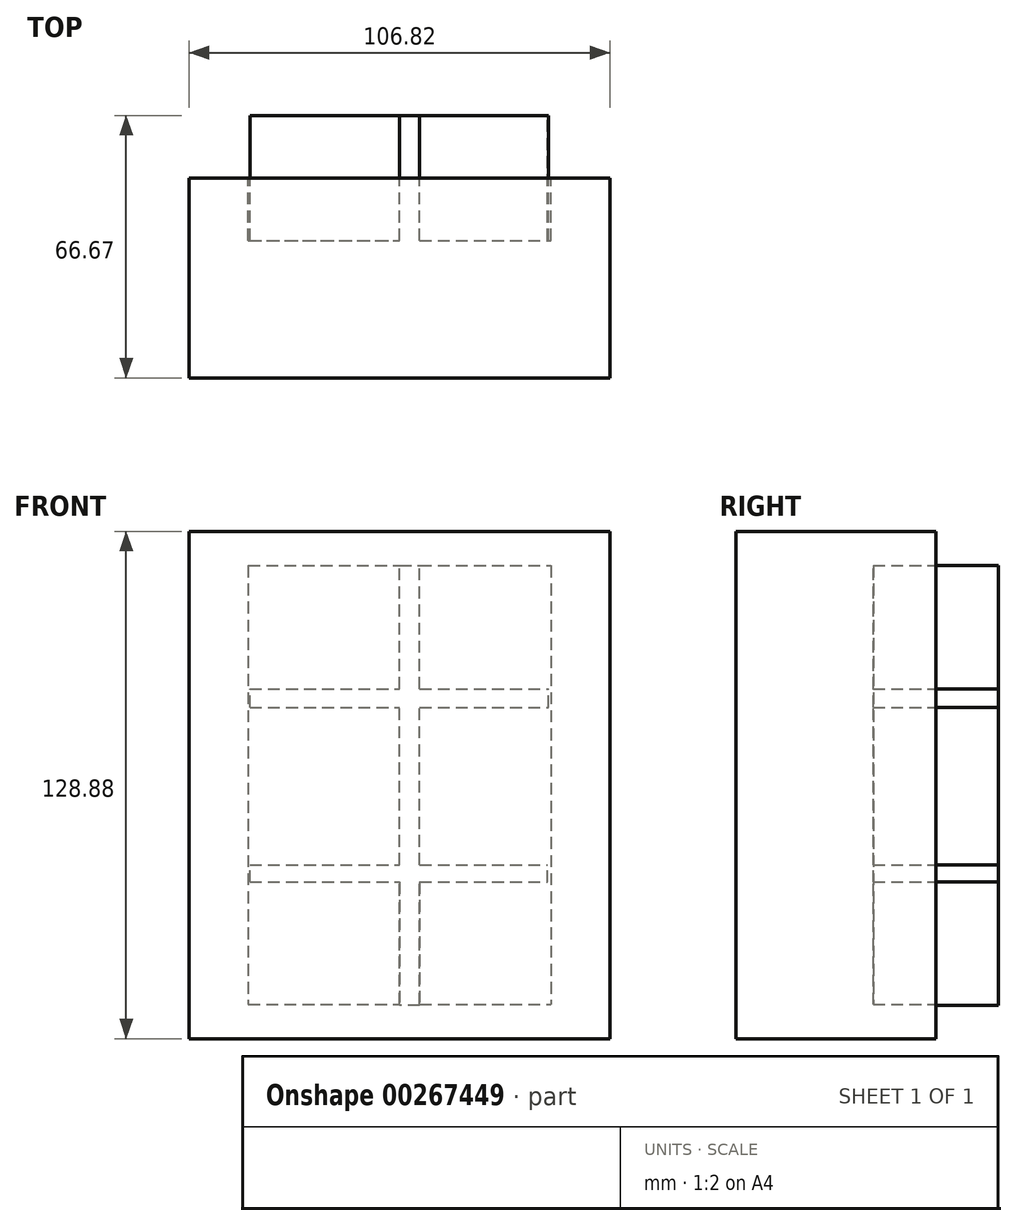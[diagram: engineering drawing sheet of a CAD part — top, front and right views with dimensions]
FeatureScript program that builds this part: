
annotation { "Feature Type Name" : "Feature", "Feature Type Description" : "" }
export const myFeature = defineFeature(function(context is Context, id is Id, definition is map)
    precondition{}
    {
        {
            var Q0;
            Q0=qCreatedBy(makeId("Front.planeOp"),FACE);
            var sketch = newSketch(context, id + "F0", { "sketchPlane" : qUnion([Q0])});
            skLineSegment(sketch, "E0.bottom", {"start": v(-38.43, 55.77) * mm, "end": v(38.43, 55.77) * mm});
            skLineSegment(sketch, "E0.top", {"start": v(-38.43, -55.77) * mm, "end": v(38.43, -55.77) * mm});
            skLineSegment(sketch, "E0.left", {"start": v(-38.43, 55.77) * mm, "end": v(-38.43, -55.77) * mm});
            skLineSegment(sketch, "E0.right", {"start": v(38.43, 55.77) * mm, "end": v(38.43, -55.77) * mm});
            skPoint(sketch, "E0.middle", {"position": v(0, 0) * mm});
            skSolve(sketch);
        }
        {
            var Q0;
            Q0 = qSketchRegion(id + "F0", true);
            extrude(context, id + "F1", {"entities" : qUnion([Q0]), "depth" : 25.4 * mm});
        }
        {
            var Q0;
            Q0=makeQuery(id+"F1.opExtrude","CAP_FACE",FACE,{"disambiguationData":[OSD([sQuery(id+"F0.wireOp",EDGE,"E0.bottom"),sQuery(id+"F0.wireOp",EDGE,"E0.top"),sQuery(id+"F0.wireOp",EDGE,"E0.left"),sQuery(id+"F0.wireOp",EDGE,"E0.right")])],"isStart":false});
            var sketch = newSketch(context, id + "F2", { "sketchPlane" : qUnion([Q0])});
            skLineSegment(sketch, "E1", {"start": v(-38.43, 23.85) * mm, "end": v(38.43, 23.85) * mm});
            skLineSegment(sketch, "E2", {"start": v(-38.43, -19.12) * mm, "end": v(38.43, -19.12) * mm});
            skLineSegment(sketch, "E3", {"start": v(0, 55.77) * mm, "end": v(0, -55.77) * mm});
            skSolve(sketch);
        }
        {
            var Q0;
            Q0 = qSketchRegion(id + "F2", true);
            var Q1;
            {var subQ0=sQuery(id+"F2.wireOp",EDGE,"E1");var subQ1=makeQuery(id+"F1.opExtrude","CAP_EDGE",EDGE,{"disambiguationData":[OSD([sQuery(id+"F0.wireOp",EDGE,"E0.left")])],"isStart":false});var subQ2=makeQuery(id+"F2.imprint","INTERSECT",VERTEX,{"derivedFrom":[subQ1,subQ0]});Q1=makeQuery(id+"F2.imprint","IMPRINT",FACE,{"disambiguationData":[TD([[makeQuery(id+"F2.imprint","IMPRINT",EDGE,{"disambiguationData":[TD([[subQ2,-1.0]])],"derivedFrom":subQ0}),1.0]])]});}
            var Q2;
            {var subQ0=sQuery(id+"F2.wireOp",EDGE,"E1");var subQ1=makeQuery(id+"F1.opExtrude","CAP_EDGE",EDGE,{"disambiguationData":[OSD([sQuery(id+"F0.wireOp",EDGE,"E0.right")])],"isStart":false});var subQ2=makeQuery(id+"F2.imprint","INTERSECT",VERTEX,{"derivedFrom":[subQ1,subQ0]});Q2=makeQuery(id+"F2.imprint","IMPRINT",FACE,{"disambiguationData":[TD([[makeQuery(id+"F2.imprint","IMPRINT",EDGE,{"disambiguationData":[TD([[subQ2,1.0]])],"derivedFrom":subQ0}),1.0]])]});}
            var Q3;
            {var subQ0=sQuery(id+"F2.wireOp",EDGE,"E1");var subQ1=makeQuery(id+"F1.opExtrude","CAP_EDGE",EDGE,{"disambiguationData":[OSD([sQuery(id+"F0.wireOp",EDGE,"E0.right")])],"isStart":false});var subQ2=makeQuery(id+"F2.imprint","INTERSECT",VERTEX,{"derivedFrom":[subQ1,subQ0]});Q3=makeQuery(id+"F2.imprint","IMPRINT",FACE,{"disambiguationData":[TD([[makeQuery(id+"F2.imprint","IMPRINT",EDGE,{"disambiguationData":[TD([[subQ2,1.0]])],"derivedFrom":subQ0}),-1.0]])]});}
            var Q4;
            {var subQ0=sQuery(id+"F2.wireOp",EDGE,"E1");var subQ1=makeQuery(id+"F1.opExtrude","CAP_EDGE",EDGE,{"disambiguationData":[OSD([sQuery(id+"F0.wireOp",EDGE,"E0.left")])],"isStart":false});var subQ2=makeQuery(id+"F2.imprint","INTERSECT",VERTEX,{"derivedFrom":[subQ1,subQ0]});Q4=makeQuery(id+"F2.imprint","IMPRINT",FACE,{"disambiguationData":[TD([[makeQuery(id+"F2.imprint","IMPRINT",EDGE,{"disambiguationData":[TD([[subQ2,-1.0]])],"derivedFrom":subQ0}),-1.0]])]});}
            var Q5;
            {var subQ0=sQuery(id+"F2.wireOp",EDGE,"E2");var subQ1=makeQuery(id+"F1.opExtrude","CAP_EDGE",EDGE,{"disambiguationData":[OSD([sQuery(id+"F0.wireOp",EDGE,"E0.left")])],"isStart":false});var subQ2=makeQuery(id+"F2.imprint","INTERSECT",VERTEX,{"derivedFrom":[subQ1,subQ0]});Q5=makeQuery(id+"F2.imprint","IMPRINT",FACE,{"disambiguationData":[TD([[makeQuery(id+"F2.imprint","IMPRINT",EDGE,{"disambiguationData":[TD([[subQ2,-1.0]])],"derivedFrom":subQ0}),-1.0]])]});}
            var Q6;
            {var subQ0=sQuery(id+"F2.wireOp",EDGE,"E2");var subQ1=makeQuery(id+"F1.opExtrude","CAP_EDGE",EDGE,{"disambiguationData":[OSD([sQuery(id+"F0.wireOp",EDGE,"E0.right")])],"isStart":false});var subQ2=makeQuery(id+"F2.imprint","INTERSECT",VERTEX,{"derivedFrom":[subQ1,subQ0]});Q6=makeQuery(id+"F2.imprint","IMPRINT",FACE,{"disambiguationData":[TD([[makeQuery(id+"F2.imprint","IMPRINT",EDGE,{"disambiguationData":[TD([[subQ2,1.0]])],"derivedFrom":subQ0}),-1.0]])]});}
            extrude(context, id + "F3", {"entities" : qUnion([Q0, Q1, Q2, Q3, Q4, Q5, Q6]), "operationType" : NewBodyOperationType.REMOVE, "oppositeDirection" : true, "depth" : 9.52 * mm});
        }
        {
            var Q0;
            Q0=makeQuery(id+"F3.boolean.opBoolean","COPY",FACE,{"derivedFrom":makeQuery(id+"F3.opExtrude","CAP_FACE",FACE,{"disambiguationData":[OSD([sQuery(id+"F0.wireOp",EDGE,"E0.bottom"),sQuery(id+"F0.wireOp",EDGE,"E0.top"),sQuery(id+"F0.wireOp",EDGE,"E0.left"),sQuery(id+"F0.wireOp",EDGE,"E0.right")])],"isStart":false})});
            var sketch = newSketch(context, id + "F4", { "sketchPlane" : qUnion([Q0])});
            skLineSegment(sketch, "E4.bottom", {"start": v(-53.4, 64.44) * mm, "end": v(53.4, 64.44) * mm});
            skLineSegment(sketch, "E4.top", {"start": v(-53.4, -64.44) * mm, "end": v(53.4, -64.44) * mm});
            skLineSegment(sketch, "E4.left", {"start": v(-53.4, 64.44) * mm, "end": v(-53.4, -64.44) * mm});
            skLineSegment(sketch, "E4.right", {"start": v(53.4, 64.44) * mm, "end": v(53.4, -64.44) * mm});
            skPoint(sketch, "E4.middle", {"position": v(0, 0) * mm});
            skSolve(sketch);
        }
        {
            var Q0;
            Q0 = qSketchRegion(id + "F4", true);
            extrude(context, id + "F5", {"entities" : qUnion([Q0]), "operationType" : NewBodyOperationType.ADD, "depth" : 50.8 * mm});
        }
        {
            var Q0;
            Q0=makeQuery(id+"F1.opExtrude","CAP_FACE",FACE,{"disambiguationData":[OSD([sQuery(id+"F0.wireOp",EDGE,"E0.bottom"),sQuery(id+"F0.wireOp",EDGE,"E0.top"),sQuery(id+"F0.wireOp",EDGE,"E0.left"),sQuery(id+"F0.wireOp",EDGE,"E0.right")])],"isStart":true});
            extrude(context, id + "F6", {"entities" : qUnion([Q0]), "operationType" : NewBodyOperationType.REMOVE, "oppositeDirection" : true, "depth" : 31.75 * mm});
        }
        {
            var Q0;
            Q0=qCreatedBy(makeId("Front.planeOp"),FACE);
            var sketch = newSketch(context, id + "F7", { "sketchPlane" : qUnion([Q0])});
            skLineSegment(sketch, "E5", {"start": v(0, 55.77) * mm, "end": v(0, -54.59) * mm});
            skLineSegment(sketch, "E6", {"start": v(37.84, 24.44) * mm, "end": v(-37.44, 24.44) * mm});
            skLineSegment(sketch, "E7", {"start": v(37.64, -20.3) * mm, "end": v(-38.63, -20.3) * mm});
            skLineSegment(sketch, "E8.bottom", {"start": v(0, 55.77) * mm, "end": v(5.12, 55.77) * mm});
            skLineSegment(sketch, "E8.top", {"start": v(0, -55.97) * mm, "end": v(5.12, -55.97) * mm});
            skLineSegment(sketch, "E8.left", {"start": v(0, 55.77) * mm, "end": v(0, -55.97) * mm});
            skLineSegment(sketch, "E8.right", {"start": v(5.12, 55.77) * mm, "end": v(5.12, -55.97) * mm});
            skLineSegment(sketch, "E9.bottom", {"start": v(37.84, 24.44) * mm, "end": v(-38.03, 24.44) * mm});
            skLineSegment(sketch, "E9.top", {"start": v(37.84, 19.7) * mm, "end": v(-38.03, 19.7) * mm});
            skLineSegment(sketch, "E9.left", {"start": v(37.84, 24.44) * mm, "end": v(37.84, 19.7) * mm});
            skLineSegment(sketch, "E9.right", {"start": v(-38.03, 24.44) * mm, "end": v(-38.03, 19.7) * mm});
            skLineSegment(sketch, "E10.bottom", {"start": v(37.64, -20.3) * mm, "end": v(-38.03, -20.3) * mm});
            skLineSegment(sketch, "E10.top", {"start": v(37.64, -24.63) * mm, "end": v(-38.03, -24.63) * mm});
            skLineSegment(sketch, "E10.left", {"start": v(37.64, -20.3) * mm, "end": v(37.64, -24.63) * mm});
            skLineSegment(sketch, "E10.right", {"start": v(-38.03, -20.3) * mm, "end": v(-38.03, -24.63) * mm});
            skSolve(sketch);
        }
        {
            var Q0;
            Q0 = qSketchRegion(id + "F7", true);
            extrude(context, id + "F8", {"entities" : qUnion([Q0]), "operationType" : NewBodyOperationType.ADD, "depth" : 50.8 * mm});
        }
    });
